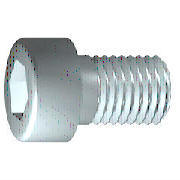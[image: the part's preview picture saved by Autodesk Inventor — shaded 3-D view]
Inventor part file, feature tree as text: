
AUTODESK INVENTOR PART (.ipt)
format: ipt  version: 2022 (Build 260153000, 153)  size: 193,536 bytes
history: native  units: mm (DEFAULTED — no unit token found)
features: sketch x2, extrude x1, plane x1, fillet x1
ambient origin geometry x7: Origin, YZ Plane, XY Plane, X Axis, Y Axis, Z Axis, Center Point
bodies: Solid1 (feature_tree), Body (feature_tree)
feature tree (5):
  extrude  "Slot"  Depth=5.0mm
  plane  "Work Plane1"
  fillet  "Fillet2"  Radius=5.0mm
  sketch  "Sketch1"  dims[d1=14.0mm d2=0.49086mm d3=5.0mm]
  sketch  "Sketch2"  dims[d4=2.5mm d5=60.0deg d6=5.0mm d7=5.0mm d8=4.618802mm d9=8.5mm d10=90.0deg d11=10.0mm d12=0.0mm d13=14.0mm d14=0.0mm d15=0.49076mm d16=0.49076mm d17=0.5mm d19=0.0mm d26=16.0mm d27=45.0deg d28=0.0mm d29=0.0mm d30=0.1mm]
